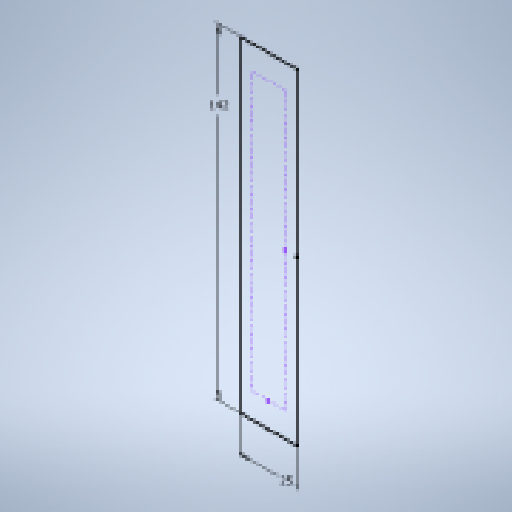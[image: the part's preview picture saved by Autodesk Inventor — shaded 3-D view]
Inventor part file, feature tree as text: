
AUTODESK INVENTOR PART (.ipt)
format: ipt  version: 2023 (Build 270158000, 158)  size: 168,960 bytes
history: native  units: mm
features: extrude x2, sketch x2
ambient origin geometry x8: Origin, YZ Plane, XZ Plane, XY Plane, X Axis, Y Axis, Z Axis, Center Point
bodies: Solid1 (feature_tree)
feature tree (4):
  extrude  "Extrusion1"  Depth=142.0mm
  extrude  "Extrusion2"  Depth=3.0mm
  sketch  "Sketch1"  dims[d0=142.0mm d1=25.0mm]
  sketch  "Sketch2"  dims[d2=131.3mm d3=15.0mm d4=5.588mm d5=3.0mm d6=0.0mm d7=12.0mm d8=24.0mm d9=53.21mm d10=27.94mm d11=39.793333mm d12=4.1656mm d13=3.0mm d14=0.0mm]
